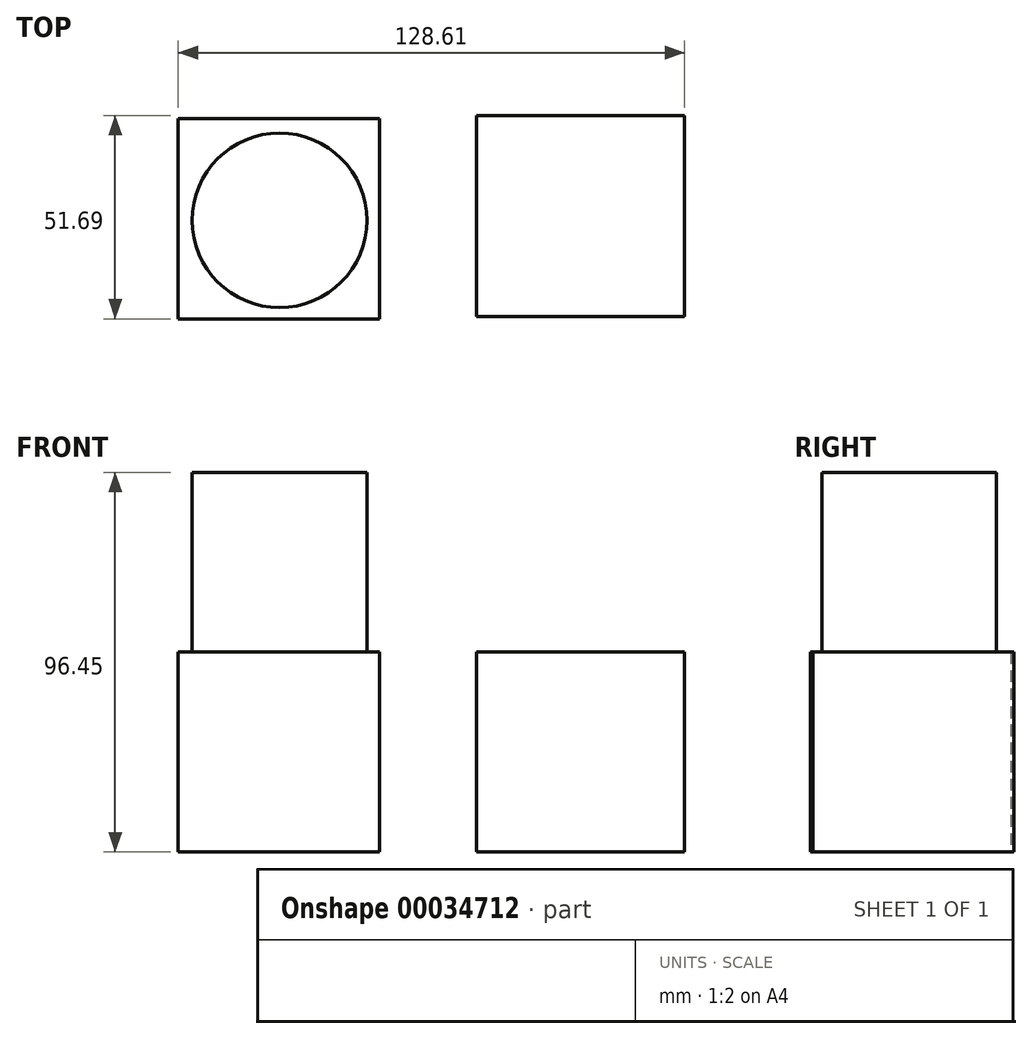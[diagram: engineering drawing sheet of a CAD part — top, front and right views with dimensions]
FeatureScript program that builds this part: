
annotation { "Feature Type Name" : "Feature", "Feature Type Description" : "" }
export const myFeature = defineFeature(function(context is Context, id is Id, definition is map)
    precondition{}
    {
        {
            var Q0;
            Q0=qCreatedBy(makeId("Top.planeOp"),FACE);
            var sketch = newSketch(context, id + "F0", { "sketchPlane" : qUnion([Q0])});
            skLineSegment(sketch, "E0.bottom", {"start": v(10.17, 11.8) * mm, "end": v(63.08, 11.8) * mm});
            skLineSegment(sketch, "E0.top", {"start": v(10.17, 62.88) * mm, "end": v(63.08, 62.88) * mm});
            skLineSegment(sketch, "E0.left", {"start": v(10.17, 11.8) * mm, "end": v(10.17, 62.88) * mm});
            skLineSegment(sketch, "E0.right", {"start": v(63.08, 11.8) * mm, "end": v(63.08, 62.88) * mm});
            skSolve(sketch);
        }
        {
            var Q0;
            Q0=qCreatedBy(makeId("Top.planeOp"),FACE);
            var sketch = newSketch(context, id + "F1", { "sketchPlane" : qUnion([Q0])});
            skLineSegment(sketch, "E1.bottom", {"start": v(-65.53, 11.2) * mm, "end": v(-14.45, 11.2) * mm});
            skLineSegment(sketch, "E1.top", {"start": v(-65.53, 62.07) * mm, "end": v(-14.45, 62.07) * mm});
            skLineSegment(sketch, "E1.left", {"start": v(-65.53, 11.2) * mm, "end": v(-65.53, 62.07) * mm});
            skLineSegment(sketch, "E1.right", {"start": v(-14.45, 11.2) * mm, "end": v(-14.45, 62.07) * mm});
            skSolve(sketch);
        }
        {
            var Q0;
            Q0=makeQuery(id+"F1.imprint","IMPRINT",FACE,{"disambiguationData":[TD([[makeQuery(id+"F1.imprint","IMPRINT",EDGE,{"derivedFrom":sQuery(id+"F1.wireOp",EDGE,"E1.bottom")}),1.0]])]});
            var sketch = newSketch(context, id + "F2", { "sketchPlane" : qUnion([Q0])});
            skCircle(sketch, "E2", {"center": v(-39.8, 36.24) * mm, "radius": 22.19 * mm});
            skSolve(sketch);
        }
        {
            var Q0;
            Q0=makeQuery(id+"F1.imprint","IMPRINT",FACE,{"disambiguationData":[TD([[makeQuery(id+"F1.imprint","IMPRINT",EDGE,{"derivedFrom":sQuery(id+"F1.wireOp",EDGE,"E1.bottom")}),1.0]])]});
            extrude(context, id + "F3", {"entities" : qUnion([Q0]), "depth" : 50.8 * mm});
        }
        {
            var Q0;
            Q0=makeQuery(id+"F2.imprint","IMPRINT",FACE,{"disambiguationData":[TD([[makeQuery(id+"F2.imprint","IMPRINT",EDGE,{"derivedFrom":sQuery(id+"F2.wireOp",EDGE,"E2")}),1.0]])]});
            extrude(context, id + "F4", {"entities" : qUnion([Q0]), "operationType" : NewBodyOperationType.ADD, "depth" : 96.45 * mm});
        }
        {
            var Q0;
            Q0=makeQuery(id+"F0.imprint","IMPRINT",FACE,{"disambiguationData":[TD([[makeQuery(id+"F0.imprint","IMPRINT",EDGE,{"derivedFrom":sQuery(id+"F0.wireOp",EDGE,"E0.bottom")}),1.0]])]});
            extrude(context, id + "F5", {"entities" : qUnion([Q0]), "depth" : 50.8 * mm});
        }
    });
